FCSTD DOCUMENT  (FreeCAD 0.21R32532 (Git))
Label: composit_stand-main-sketches
License: All rights reserved
LicenseURL: http://en.wikipedia.org/wiki/All_rights_reserved
objects: Sketcher::SketchObject×1, Spreadsheet::Sheet×1
note: 1 computed .brp shape members not serialized (recipe doc carries the construction recipe); baked Part::Feature solids carry a one-line shape summary decoded from their .brp
EXTERNAL_REF file=composit-properties.FCStd obj=Spreadsheet

FEATURE [Sketcher::SketchObject] Sketch
  FullyConstrained = true
  expr: Constraints[31] = <<Properties>>.end_face_width
  sketch-geometry (13):
    g0: LineSegment StartX=14.5 StartY=8.37158 StartZ=0 EndX=14.5 EndY=18.3716 EndZ=0
    g1: LineSegment StartX=14.5 StartY=18.3716 StartZ=0 EndX=-14.5 EndY=18.3716 EndZ=0
    g2: LineSegment StartX=-14.5 StartY=18.3716 StartZ=0 EndX=-14.5 EndY=8.37158 EndZ=0
    g3: LineSegment StartX=-14.5 StartY=8.37158 StartZ=0 EndX=-23.1603 EndY=3.37158 EndZ=0
    g4: LineSegment StartX=-23.1603 StartY=3.37158 StartZ=0 EndX=-8.66025 EndY=-21.7432 EndZ=0
    g5: LineSegment StartX=-8.66025 StartY=-21.7432 StartZ=0 EndX=0 EndY=-16.7432 EndZ=0
    g6: LineSegment StartX=0 StartY=-16.7432 StartZ=0 EndX=8.66025 EndY=-21.7432 EndZ=0
    g7: LineSegment StartX=8.66025 StartY=-21.7432 StartZ=0 EndX=23.1603 EndY=3.37158 EndZ=0
    g8: LineSegment StartX=23.1603 StartY=3.37158 StartZ=0 EndX=14.5 EndY=8.37158 EndZ=0
    g9: LineSegment StartX=0 StartY=0 StartZ=0 EndX=0 EndY=-16.7432 EndZ=0
    g10: LineSegment StartX=0 StartY=0 StartZ=0 EndX=-14.5 EndY=8.37158 EndZ=0
    g11: LineSegment StartX=0 StartY=0 StartZ=0 EndX=14.5 EndY=8.37158 EndZ=0
    g12: GeomPoint X=0 Y=8.37158 Z=0
  constraints (36):
    c: Coincident(g0,g1)
    c: Coincident(g1,g2)
    c: Coincident(g2,g3)
    c: Coincident(g3,g4)
    c: Coincident(g4,g5)
    c: PointOnObject(g5,g-2)
    c: Coincident(g5,g6)
    c: Coincident(g6,g7)
    c: Coincident(g7,g8)
    c: Perpendicular(g1,g0)
    c: Perpendicular(g2,g1)
    c: Perpendicular(g4,g5)
    c: Perpendicular(g3,g4)
    c: Perpendicular(g7,g6)
    c: Perpendicular(g8,g7)
    c: Equal(g7,g4)
    c: Equal(g4,g1)
    c: Equal(g2,g3)
    c: Equal(g3,g6)
    c: Coincident(g9,g-1)
    c: Coincident(g9,g5)
    c: Coincident(g10,g9)
    c: Coincident(g10,g2)
    c: Coincident(g11,g9)
    c: Equal(g10,g9)
    c: Equal(g5,g3)
    c: Symmetric(g0,g1,g-2)
    c: Coincident(g8,g0)
    c: Coincident(g11,g0)
    c: Equal(g8,g2)
    c: DistanceY(g0,g0) = 10
    c: DistanceX(g1,g1) = 29
    c: DistanceY(g9,g9) = 16.7432  'connection_offset'
    c: PointOnObject(g12,g-2)
    c: Horizontal(g12,g0)
    c: DistanceY(g12) = 8.37158  'petal_offset'
FEATURE [Spreadsheet::Sheet] Spreadsheet  label="Properties"
  cells = B2(end_face_width)==29 mm; C2(inner_width)==end_face_width - <<composit-properties>>#<<Properties>>.thickness * 2
